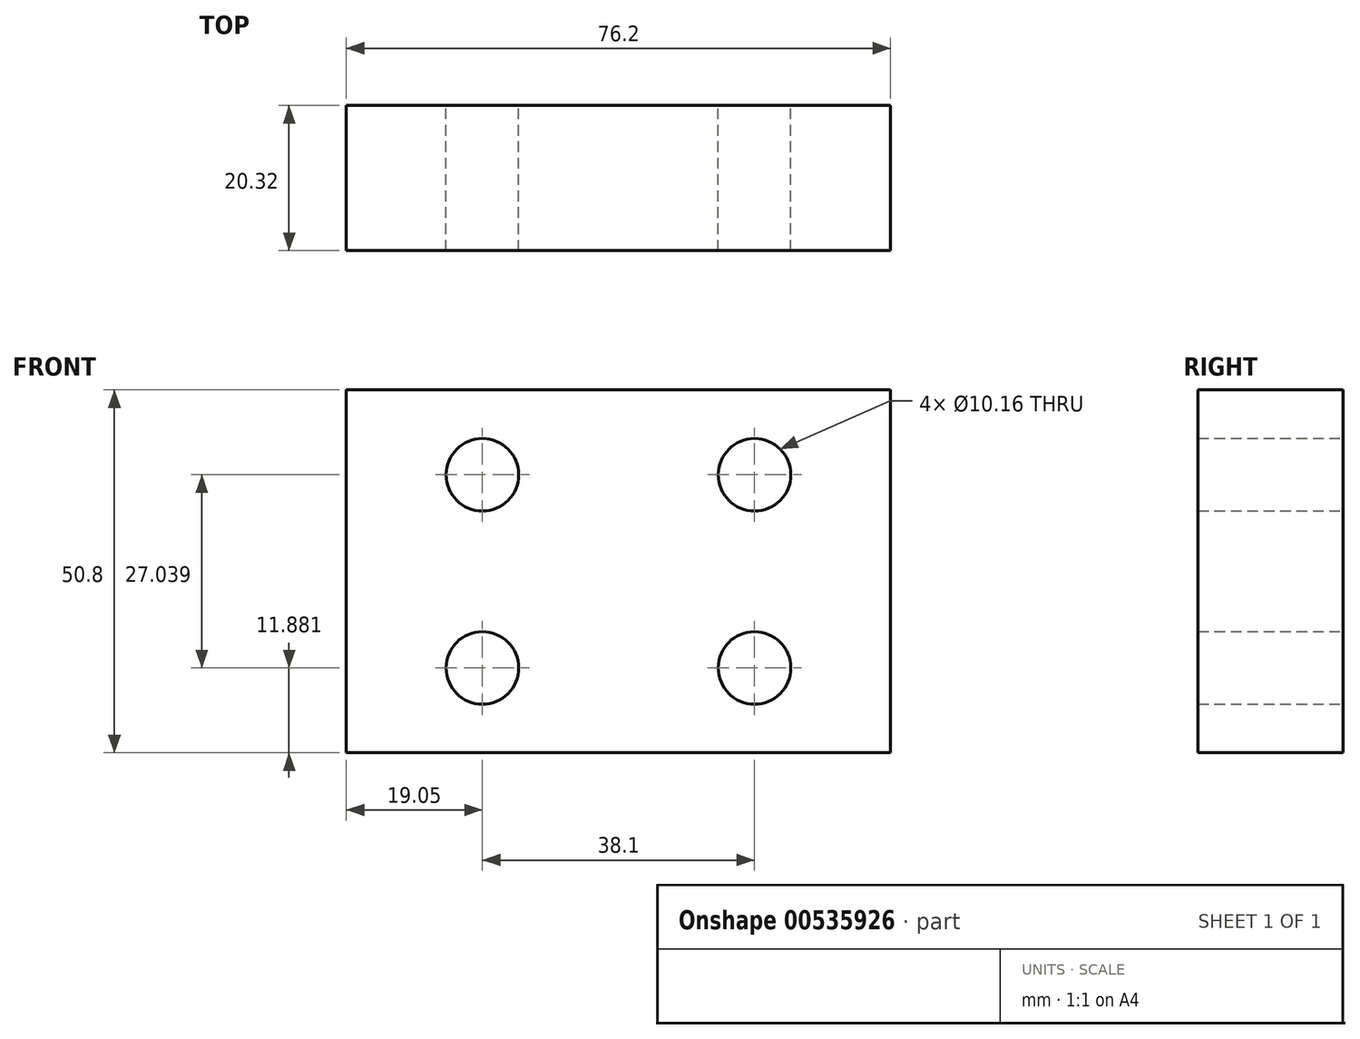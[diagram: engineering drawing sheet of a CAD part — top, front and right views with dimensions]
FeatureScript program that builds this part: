
annotation { "Feature Type Name" : "Feature", "Feature Type Description" : "" }
export const myFeature = defineFeature(function(context is Context, id is Id, definition is map)
    precondition{}
    {
        {
            var Q0;
            Q0=qCreatedBy(makeId("Front.planeOp"),FACE);
            var sketch = newSketch(context, id + "F0", { "sketchPlane" : qUnion([Q0])});
            skLineSegment(sketch, "E0.bottom", {"start": v(-38.1, 25.4) * mm, "end": v(38.1, 25.4) * mm});
            skLineSegment(sketch, "E0.top", {"start": v(-38.1, -25.4) * mm, "end": v(38.1, -25.4) * mm});
            skLineSegment(sketch, "E0.left", {"start": v(-38.1, 25.4) * mm, "end": v(-38.1, -25.4) * mm});
            skLineSegment(sketch, "E0.right", {"start": v(38.1, 25.4) * mm, "end": v(38.1, -25.4) * mm});
            skCircle(sketch, "E1", {"center": v(-19.05, 13.52) * mm, "radius": 5.08 * mm});
            skCircle(sketch, "E2", {"center": v(-19.05, -13.52) * mm, "radius": 5.08 * mm});
            skCircle(sketch, "E3", {"center": v(19.05, 13.52) * mm, "radius": 5.08 * mm});
            skCircle(sketch, "E4", {"center": v(19.05, -13.52) * mm, "radius": 5.08 * mm});
            skSolve(sketch);
        }
        {
            var Q0;
            Q0=makeQuery(id+"F0.imprint","IMPRINT",FACE,{"disambiguationData":[TD([[makeQuery(id+"F0.imprint","IMPRINT",EDGE,{"derivedFrom":sQuery(id+"F0.wireOp",EDGE,"E0.bottom")}),-1.0]])]});
            extrude(context, id + "F1", {"entities" : qUnion([Q0]), "depth" : 20.32 * mm, "offsetDistance" : 25.4 * mm});
        }
    });
